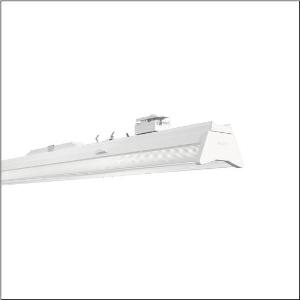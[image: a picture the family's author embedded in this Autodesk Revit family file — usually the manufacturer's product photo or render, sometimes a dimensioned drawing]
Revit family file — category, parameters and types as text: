
# Revit family: licross_r__11_performance_mo_51td16mn4axg_aad5
name_source: partatom
category: Lighting Fixtures
units: mm (PartAtom-declared; Revit-internal decimal feet)

## family parameters
Cut with Voids When Loaded = No
Host = Face
Light Source = No
Part Type = Normal
Room Calculation Point = No
Round Connector Dimension = Use Diameter
Shared = No

## types (1)
- --- (1 x LED, 10160 lm, 55.3 W, 4000K)
    Apparent Load = 55 VA
    CIE Flux Codes = 66 88 96 79 100
    Color Rendering = 80
    Color Temperature = 4000K
    Default Elevation = 1800 mm
    Description = Licross® 11 Performance MO, luminaire insert, of sheet steel, galvanised, coil coated, white, length: 1.500mm, width: 120mm, height: 123mm, LED rated luminous flux: 10.160lm, light colour: 840, control gear: ON/OFF Multilumen, with plug, 3-pole, with phase selection, mains connection: 220..240V, AC, 50/60Hz, rated input power: 55W, halogen-free wiring, primary light control with lens, of plastic, primary optical cover: cover, of PMMA, light emission: direct/indirect distribution, primary light characteristic: symmetric, protection rating (complete): IP54, insulation class (complete): insulation class I (protective earthing), certification: CE, ENEC, VDE, UKCA, protection symbol: D if used in an environment with non-conductive dust loads with corresponding accessories, impact resistance: IK06, permissible ambient temperature for indoor applications: -35..+40°C, corresponds to IFS (International Featured Standards) requirements for safety and quality in the food industry, reducing of maximum allowable ambient temperature of 5°C with ceiling mounting, LABS conformity tested according to VDMA 24364:2018-05, packaging unit: 1 piece
    Height = 114 mm
    Lamp = 1 x LED
    Lamp Light Flux = 10160 lm
    Lamp Power = 55.3 W
    Lamp count = 1
    Length = 1500 mm
    Luminous efficacy = 184 lm/W
    Manufacturer = Siteco
    ModVariant = No
    Model = 51TD16MN4AXG
    Mounting Place = Ceiling
    Mounting Type = Pendant
    Number of Poles = 1
    OnlyDefault = Yes
    Power Factor = 1
    Product Name = Licross® 11 Performance MO
    Product group = luminaire insert
    ProductGroupID = 901
    Protection Class = Protection class I
    Protection Degree = IP 54
    RLX_Detail_Level = 1
    RLX_Emergency_Light_Flux = 0 lm
    RLX_Emergency_Type = 0
    RLX_Emergency_Type_DB = No
    RlxData = <blob elided: 31769 chars, md5=87598a0f>
    Socket = socket
    Standby Power = 0 W
    System Light Flux = 10160 lm
    System Power = 55 W
    Type Comments = factory setting: luminous flux: 100 % | (A | C | E) | 126 mA
    Type Image = l_1256138.jpg
    URL = http://relux.com
    VarID = @adj_038305
    Voltage = 0 V
    Weight = 0.00 kg
    Width = 120 mm

## geometry (parser evidence)
native form markers: Blend x4, Sweep x13
no freeform markers — native parametric forms only
